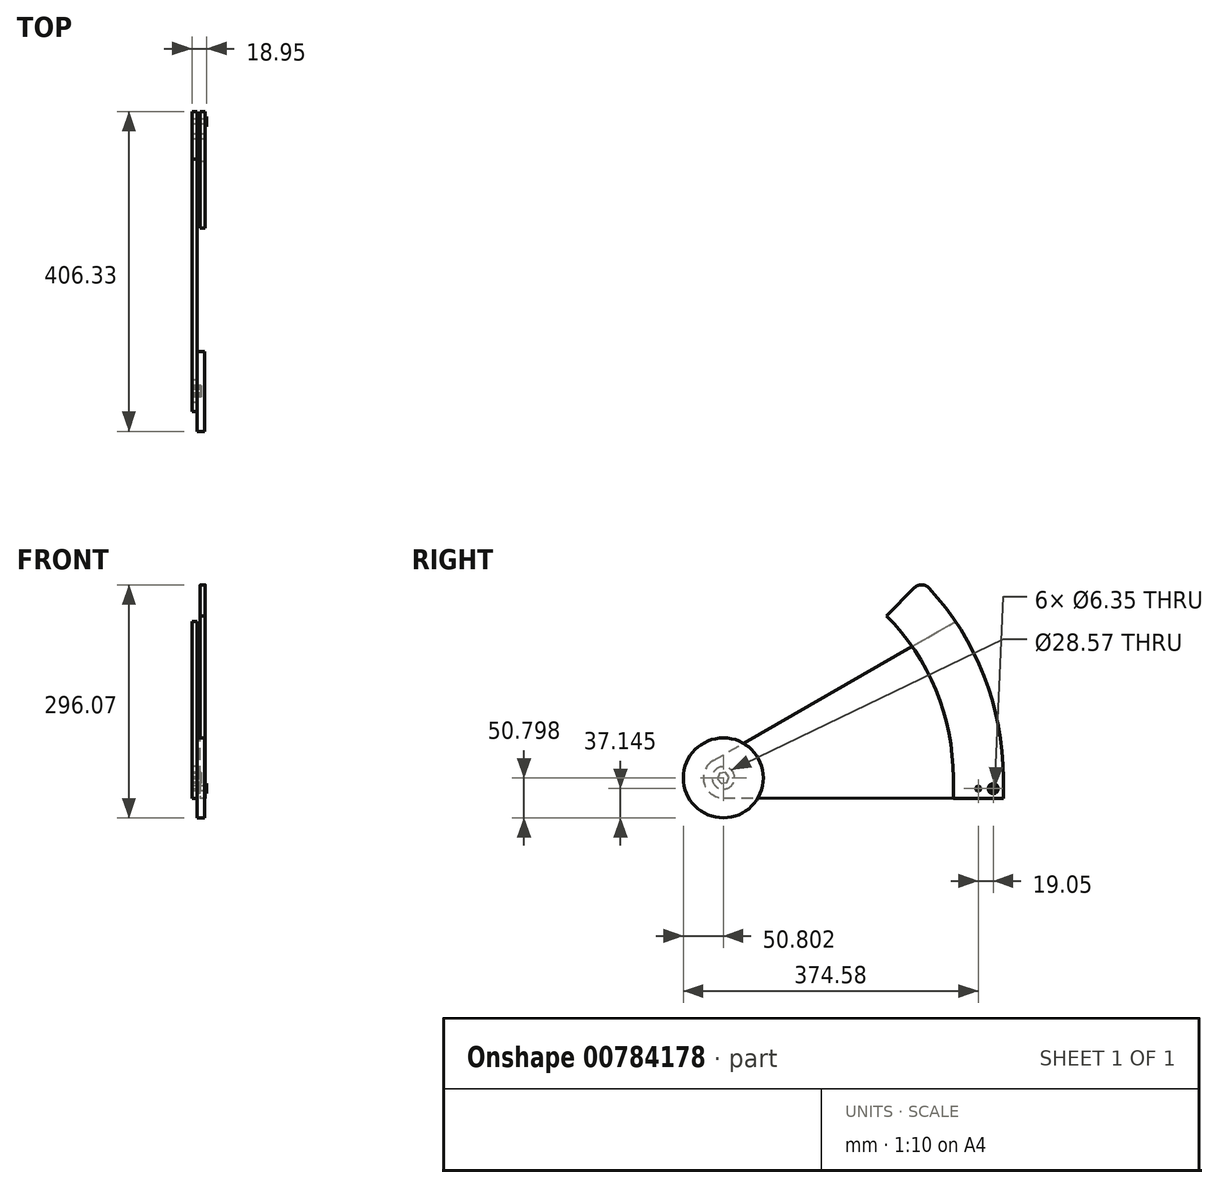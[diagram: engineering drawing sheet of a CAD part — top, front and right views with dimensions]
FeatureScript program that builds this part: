
annotation { "Feature Type Name" : "Feature", "Feature Type Description" : "" }
export const myFeature = defineFeature(function(context is Context, id is Id, definition is map)
    precondition{}
    {
        {
            assignVariable(context, id + "F0", {"name" : "rail_width", "anyValue" : 2});
        }
        {
            assignVariable(context, id + "F1", {"name" : "game_piece_diameter", "anyValue" : 10});
        }
        {
            var Q0;
            Q0=qCreatedBy(makeId("Right.planeOp"),FACE);
            var sketch = newSketch(context, id + "F2", { "sketchPlane" : qUnion([Q0])});
            skLineSegment(sketch, "E0", {"start": v(-355.6, 0.99) * mm, "end": v(0, 0) * mm});
            skArc(sketch, "E1.filletArc", {"start": v(-368.33, 48.33) * mm, "mid": v(-380.06, 19.8) * mm, "end": v(-355.6, 0.99) * mm});
            skCircle(sketch, "E2", {"center": v(-355.53, 26.39) * mm, "radius": 14.29 * mm});
            skArc(sketch, "E3", {"start": v(0, 26.39) * mm, "mid": v(-15.48, 130.15) * mm, "end": v(-60.57, 224.88) * mm});
            skLineSegment(sketch, "E4", {"start": v(-368.33, 48.33) * mm, "end": v(-60.57, 224.88) * mm});
            skLineSegment(sketch, "E5", {"start": v(0, 0) * mm, "end": v(0, 26.39) * mm});
            skSolve(sketch);
        }
        {
            var Q0;
            Q0 = qSketchRegion(id + "F2", true);
            extrude(context, id + "F3", {"entities" : qUnion([Q0]), "depth" : 6.35 * mm, "offsetDistance" : 25.4 * mm});
        }
        {
            var Q0;
            Q0=makeQuery(id+"F3.opExtrude","CAP_FACE",FACE,{"disambiguationData":[OSD([sQuery(id+"F2.wireOp",EDGE,"E0"),sQuery(id+"F2.wireOp",EDGE,"E1.filletArc"),sQuery(id+"F2.wireOp",EDGE,"E2"),sQuery(id+"F2.wireOp",EDGE,"E3"),sQuery(id+"F2.wireOp",EDGE,"E4"),sQuery(id+"F2.wireOp",EDGE,"E5")])],"isStart":true});
            var sketch = newSketch(context, id + "F4", { "sketchPlane" : qUnion([Q0])});
            skCircle(sketch, "E6.cCircle", {"center": v(355.53, 26.39) * mm, "radius": 6.35 * mm, "construction": true});
            skLineSegment(sketch, "E6.0", {"start": v(362.74, 25.09) * mm, "end": v(358, 19.49) * mm});
            skLineSegment(sketch, "E6.1", {"start": v(358, 19.49) * mm, "end": v(350.8, 20.8) * mm});
            skLineSegment(sketch, "E6.2", {"start": v(350.8, 20.8) * mm, "end": v(348.31, 27.7) * mm});
            skLineSegment(sketch, "E6.3", {"start": v(348.31, 27.7) * mm, "end": v(353.05, 33.29) * mm});
            skLineSegment(sketch, "E6.4", {"start": v(353.05, 33.29) * mm, "end": v(360.26, 31.99) * mm});
            skLineSegment(sketch, "E6.5", {"start": v(360.26, 31.99) * mm, "end": v(362.74, 25.09) * mm});
            skPoint(sketch, "E6.0.midPoint", {"position": v(360.38, 22.29) * mm});
            skSolve(sketch);
        }
        {
            var Q0;
            Q0 = qSketchRegion(id + "F4", true);
            extrude(context, id + "F5", {"entities" : qUnion([Q0]), "oppositeDirection" : true, "depth" : (getVariable(context, 'game_piece_diameter') + 1.5) * mm, "offsetDistance" : 25.4 * mm});
        }
        {
            var Q0;
            Q0=makeQuery(id+"F3.opExtrude","CAP_FACE",FACE,{"disambiguationData":[OSD([sQuery(id+"F2.wireOp",EDGE,"E0"),sQuery(id+"F2.wireOp",EDGE,"E1.filletArc"),sQuery(id+"F2.wireOp",EDGE,"E2"),sQuery(id+"F2.wireOp",EDGE,"E3"),sQuery(id+"F2.wireOp",EDGE,"E4"),sQuery(id+"F2.wireOp",EDGE,"E5")])],"isStart":false});
            var sketch = newSketch(context, id + "F6", { "sketchPlane" : qUnion([Q0])});
            skCircle(sketch, "E7", {"center": v(-12.7, 12.74) * mm, "radius": 6.35 * mm});
            skCircle(sketch, "E8.0", {"center": v(-12.7, 12.74) * mm, "radius": 3.18 * mm});
            skSolve(sketch);
        }
        {
            var Q0;
            Q0 = qSketchRegion(id + "F6", true);
            extrude(context, id + "F7", {"entities" : qUnion([Q0]), "depth" : ((getVariable(context, 'game_piece_diameter') + 1 - getVariable(context, 'rail_width') - 0.5) / 2) * mm, "offsetDistance" : 25.4 * mm});
        }
        {
            var Q0;
            Q0=makeQuery(id+"F7.opExtrude","CAP_FACE",FACE,{"disambiguationData":[OSD([sQuery(id+"F6.wireOp",EDGE,"E7"),sQuery(id+"F6.wireOp",EDGE,"E8.0")])],"isStart":false});
            var sketch = newSketch(context, id + "F8", { "sketchPlane" : qUnion([Q0])});
            skArc(sketch, "E9", {"start": v(-63.43, 26.39) * mm, "mid": v(-85.5, 137.8) * mm, "end": v(-148.4, 232.36) * mm});
            skArc(sketch, "E10", {"start": v(0, 26.39) * mm, "mid": v(-24.42, 155.87) * mm, "end": v(-94.32, 267.57) * mm});
            skLineSegment(sketch, "E11", {"start": v(0, 26.39) * mm, "end": v(0, 0) * mm});
            skLineSegment(sketch, "E12", {"start": v(-63.43, 26.39) * mm, "end": v(-63.43, 0) * mm});
            skLineSegment(sketch, "E13", {"start": v(-63.43, 0) * mm, "end": v(0, 0) * mm});
            skLineSegment(sketch, "E14", {"start": v(-112.6, 267.96) * mm, "end": v(-148.4, 232.36) * mm});
            skPoint(sketch, "E15.visualSharp", {"position": v(-103.43, 277.08) * mm});
            skArc(sketch, "E15.filletArc", {"start": v(-94.32, 267.57) * mm, "mid": v(-103.38, 271.66) * mm, "end": v(-112.6, 267.96) * mm});
            skSolve(sketch);
        }
        {
            var Q0;
            Q0 = qSketchRegion(id + "F8", true);
            extrude(context, id + "F9", {"entities" : qUnion([Q0]), "depth" : 6.35 * mm, "offsetDistance" : 25.4 * mm});
        }
        {
            var Q0;
            Q0=makeQuery(id+"F9.opExtrude","CAP_FACE",FACE,{"disambiguationData":[OSD([sQuery(id+"F8.wireOp",EDGE,"E9"),sQuery(id+"F8.wireOp",EDGE,"E10"),sQuery(id+"F8.wireOp",EDGE,"E11"),sQuery(id+"F8.wireOp",EDGE,"E12"),sQuery(id+"F8.wireOp",EDGE,"E13"),sQuery(id+"F8.wireOp",EDGE,"E14"),sQuery(id+"F8.wireOp",EDGE,"E15.filletArc")])],"isStart":false});
            var sketch = newSketch(context, id + "F10", { "sketchPlane" : qUnion([Q0])});
            skCircle(sketch, "E16", {"center": v(-12.7, 12.74) * mm, "radius": 3.17 * mm});
            skCircle(sketch, "E17", {"center": v(-12.7, 12.74) * mm, "radius": 6.35 * mm});
            skSolve(sketch);
        }
        {
            var Q0;
            Q0 = qSketchRegion(id + "F10", true);
            extrude(context, id + "F11", {"entities" : qUnion([Q0]), "depth" : (getVariable(context, 'rail_width')) * mm, "offsetDistance" : 25.4 * mm});
        }
        {
            var Q0;
            Q0=makeQuery(id+"F3.opExtrude","CAP_FACE",FACE,{"disambiguationData":[OSD([sQuery(id+"F2.wireOp",EDGE,"E0"),sQuery(id+"F2.wireOp",EDGE,"E1.filletArc"),sQuery(id+"F2.wireOp",EDGE,"E2"),sQuery(id+"F2.wireOp",EDGE,"E3"),sQuery(id+"F2.wireOp",EDGE,"E4"),sQuery(id+"F2.wireOp",EDGE,"E5")])],"isStart":true});
            var sketch = newSketch(context, id + "F12", { "sketchPlane" : qUnion([Q0])});
            skCircle(sketch, "E18", {"center": v(12.7, 12.74) * mm, "radius": 3.17 * mm});
            skPoint(sketch, "E19.center", {"position": v(355.53, 26.39) * mm});
            skCircle(sketch, "E20", {"center": v(31.75, 12.74) * mm, "radius": 3.18 * mm});
            skSolve(sketch);
        }
        {
            var Q0;
            Q0 = qSketchRegion(id + "F12", true);
            extrude(context, id + "F13", {"entities" : qUnion([Q0]), "operationType" : NewBodyOperationType.REMOVE, "endBound" : BoundingType.THROUGH_ALL, "oppositeDirection" : true, "depth" : 25.4 * mm, "offsetDistance" : 25.4 * mm});
        }
        {
            var Q0;
            Q0=makeQuery(id+"F3.opExtrude","CAP_FACE",FACE,{"disambiguationData":[OSD([sQuery(id+"F2.wireOp",EDGE,"E0"),sQuery(id+"F2.wireOp",EDGE,"E1.filletArc"),sQuery(id+"F2.wireOp",EDGE,"E2"),sQuery(id+"F2.wireOp",EDGE,"E3"),sQuery(id+"F2.wireOp",EDGE,"E4"),sQuery(id+"F2.wireOp",EDGE,"E5")])],"isStart":false});
            var sketch = newSketch(context, id + "F14", { "sketchPlane" : qUnion([Q0])});
            skCircle(sketch, "E21", {"center": v(-355.53, 26.39) * mm, "radius": 50.8 * mm});
            skSolve(sketch);
        }
        {
            var Q0;
            Q0 = qSketchRegion(id + "F14", true);
            extrude(context, id + "F15", {"entities" : qUnion([Q0]), "depth" : (getVariable(context, 'game_piece_diameter')) * mm, "offsetDistance" : 25.4 * mm});
        }
    });
